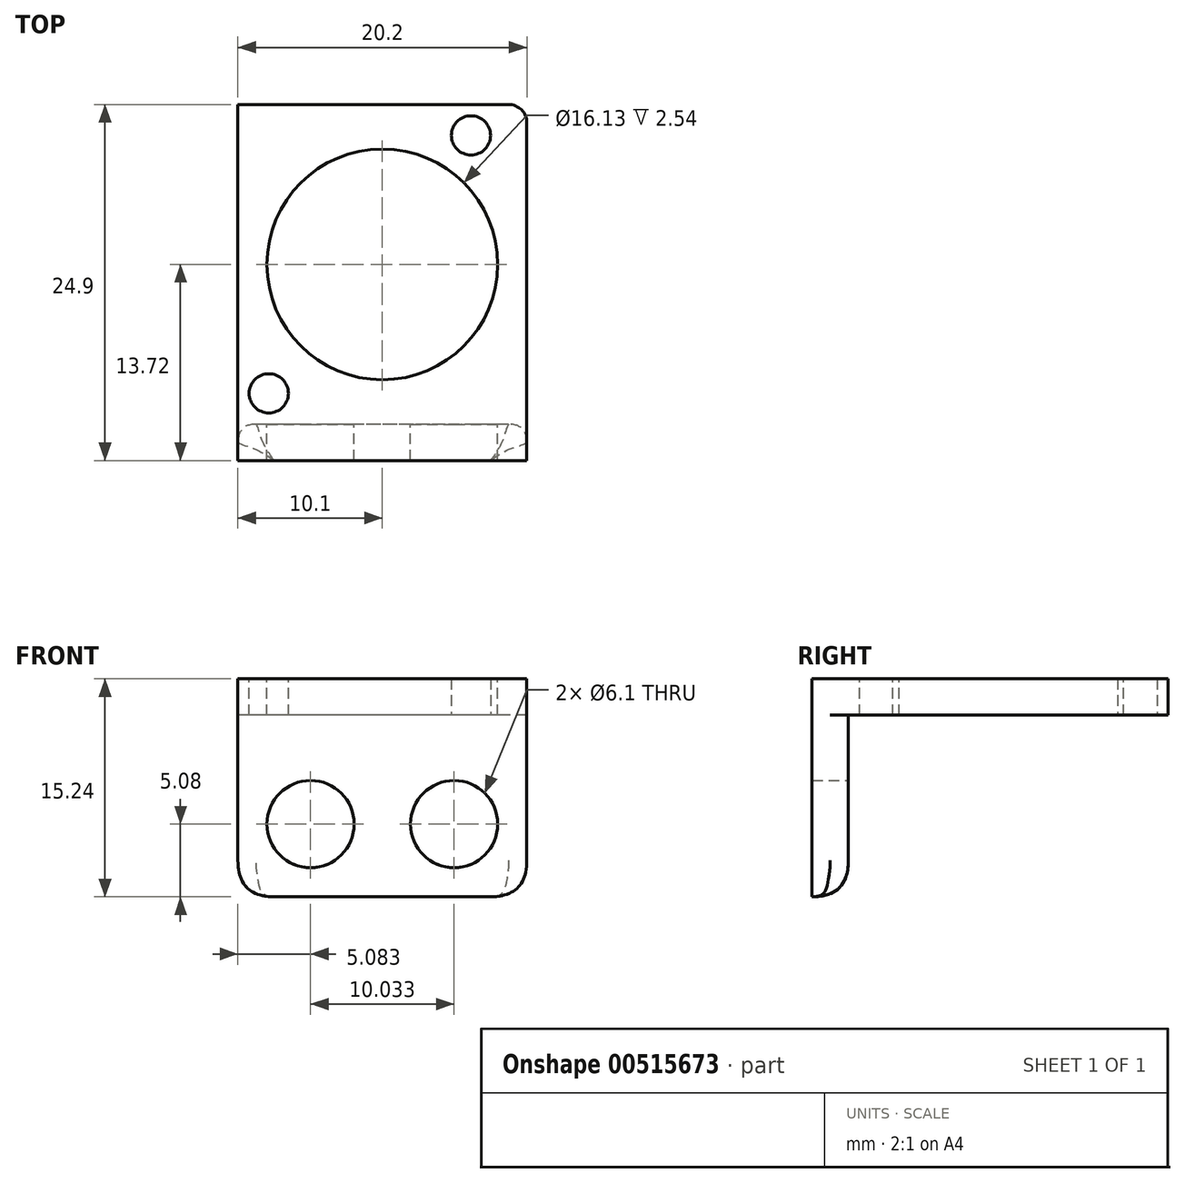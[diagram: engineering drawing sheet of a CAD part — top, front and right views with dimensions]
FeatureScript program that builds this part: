
annotation { "Feature Type Name" : "Feature", "Feature Type Description" : "" }
export const myFeature = defineFeature(function(context is Context, id is Id, definition is map)
    precondition{}
    {
        {
            var Q0;
            Q0=qCreatedBy(makeId("Top.planeOp"),FACE);
            var sketch = newSketch(context, id + "F0", { "sketchPlane" : qUnion([Q0])});
            skLineSegment(sketch, "E0.bottom", {"start": v(10.1, 11.18) * mm, "end": v(-10.1, 11.18) * mm});
            skLineSegment(sketch, "E0.top", {"start": v(10.1, -11.18) * mm, "end": v(-10.1, -11.18) * mm});
            skLineSegment(sketch, "E0.left", {"start": v(10.1, 11.18) * mm, "end": v(10.1, -11.18) * mm});
            skLineSegment(sketch, "E0.right", {"start": v(-10.1, 11.18) * mm, "end": v(-10.1, -11.18) * mm});
            skPoint(sketch, "E0.middle", {"position": v(0, 0) * mm});
            skSolve(sketch);
        }
        {
            var Q0;
            Q0=makeQuery(id+"F0.imprint","IMPRINT",FACE,{"disambiguationData":[TD([[makeQuery(id+"F0.imprint","IMPRINT",EDGE,{"derivedFrom":sQuery(id+"F0.wireOp",EDGE,"E0.bottom")}),1.0]])]});
            var sketch = newSketch(context, id + "F1", { "sketchPlane" : qUnion([Q0])});
            skCircle(sketch, "E1", {"center": v(6.2, 9.02) * mm, "radius": 1.37 * mm});
            skSolve(sketch);
        }
        {
            var Q0;
            Q0=makeQuery(id+"F1.imprint","IMPRINT",FACE,{"disambiguationData":[TD([[makeQuery(id+"F1.imprint","IMPRINT",EDGE,{"derivedFrom":sQuery(id+"F1.wireOp",EDGE,"E1")}),-1.0]])]});
            extrude(context, id + "F2", {"entities" : qUnion([Q0]), "depth" : 2.54 * mm, "offsetDistance" : 25.4 * mm});
        }
        {
            var Q0;
            Q0=makeQuery(id+"F2.opExtrude","CAP_FACE",FACE,{"disambiguationData":[OSD([sQuery(id+"F0.wireOp",EDGE,"E0.bottom"),sQuery(id+"F0.wireOp",EDGE,"E0.top"),sQuery(id+"F0.wireOp",EDGE,"E0.left"),sQuery(id+"F0.wireOp",EDGE,"E0.right"),sQuery(id+"F1.wireOp",EDGE,"E1")])],"isStart":false});
            var sketch = newSketch(context, id + "F3", { "sketchPlane" : qUnion([Q0])});
            skCircle(sketch, "E2", {"center": v(-7.94, -9.02) * mm, "radius": 1.37 * mm});
            skSolve(sketch);
        }
        {
            var Q0;
            Q0=makeQuery(id+"F3.imprint","IMPRINT",FACE,{"disambiguationData":[TD([[makeQuery(id+"F3.imprint","IMPRINT",EDGE,{"derivedFrom":sQuery(id+"F3.wireOp",EDGE,"E2")}),1.0]])]});
            extrude(context, id + "F4", {"entities" : qUnion([Q0]), "operationType" : NewBodyOperationType.REMOVE, "oppositeDirection" : true, "depth" : 2.54 * mm, "offsetDistance" : 25.4 * mm});
        }
        {
            var Q0;
            Q0=makeQuery(id+"F2.opExtrude","CAP_FACE",FACE,{"disambiguationData":[OSD([sQuery(id+"F0.wireOp",EDGE,"E0.bottom"),sQuery(id+"F0.wireOp",EDGE,"E0.top"),sQuery(id+"F0.wireOp",EDGE,"E0.left"),sQuery(id+"F0.wireOp",EDGE,"E0.right"),sQuery(id+"F1.wireOp",EDGE,"E1")])],"isStart":false});
            var sketch = newSketch(context, id + "F5", { "sketchPlane" : qUnion([Q0])});
            skCircle(sketch, "E3", {"center": v(0, 0) * mm, "radius": 8.06 * mm});
            skSolve(sketch);
        }
        {
            var Q0;
            Q0=makeQuery(id+"F5.imprint","IMPRINT",FACE,{"disambiguationData":[TD([[makeQuery(id+"F5.imprint","IMPRINT",EDGE,{"derivedFrom":sQuery(id+"F5.wireOp",EDGE,"E3")}),1.0]])]});
            extrude(context, id + "F6", {"entities" : qUnion([Q0]), "operationType" : NewBodyOperationType.REMOVE, "oppositeDirection" : true, "depth" : 2.54 * mm, "offsetDistance" : 25.4 * mm});
        }
        {
            var Q0;
            Q0=makeQuery(id+"F2.opExtrude","SWEPT_EDGE",EDGE,{"disambiguationData":[OSD([sQuery(id+"F0.wireOp",EDGE,"E0.bottom"),sQuery(id+"F0.wireOp",EDGE,"E0.left")])]});
            fillet(context, id + "F7", {"entities" : qUnion([Q0]), "radius" : 1.27 * mm, "tangentPropagation" : true, "allowEdgeOverflow" : false});
        }
        {
            var Q0;
            Q0=makeQuery(id+"F2.opExtrude","CAP_FACE",FACE,{"disambiguationData":[OSD([sQuery(id+"F0.wireOp",EDGE,"E0.bottom"),sQuery(id+"F0.wireOp",EDGE,"E0.top"),sQuery(id+"F0.wireOp",EDGE,"E0.left"),sQuery(id+"F0.wireOp",EDGE,"E0.right"),sQuery(id+"F1.wireOp",EDGE,"E1")])],"isStart":false});
            var sketch = newSketch(context, id + "F8", { "sketchPlane" : qUnion([Q0])});
            skLineSegment(sketch, "E4.bottom", {"start": v(-10.1, -11.18) * mm, "end": v(10.1, -11.18) * mm});
            skLineSegment(sketch, "E4.top", {"start": v(-10.1, -13.72) * mm, "end": v(10.1, -13.72) * mm});
            skLineSegment(sketch, "E4.left", {"start": v(-10.1, -11.18) * mm, "end": v(-10.1, -13.72) * mm});
            skLineSegment(sketch, "E4.right", {"start": v(10.1, -11.18) * mm, "end": v(10.1, -13.72) * mm});
            skSolve(sketch);
        }
        {
            var Q0;
            Q0=makeQuery(id+"F8.imprint","IMPRINT",FACE,{"disambiguationData":[TD([[makeQuery(id+"F8.imprint","IMPRINT",EDGE,{"derivedFrom":sQuery(id+"F8.wireOp",EDGE,"E4.top")}),1.0]])]});
            extrude(context, id + "F9", {"entities" : qUnion([Q0]), "operationType" : NewBodyOperationType.ADD, "oppositeDirection" : true, "depth" : 15.24 * mm, "offsetDistance" : 25.4 * mm});
        }
        {
            var Q0;
            Q0=makeQuery(id+"F9.opExtrude","SWEPT_FACE",FACE,{"disambiguationData":[OSD([sQuery(id+"F8.wireOp",EDGE,"E4.bottom")])]});
            var sketch = newSketch(context, id + "F10", { "sketchPlane" : qUnion([Q0])});
            skCircle(sketch, "E5", {"center": v(-5.02, -7.62) * mm, "radius": 3.05 * mm});
            skSolve(sketch);
        }
        {
            var Q0;
            Q0=makeQuery(id+"F10.imprint","IMPRINT",FACE,{"disambiguationData":[TD([[makeQuery(id+"F10.imprint","IMPRINT",EDGE,{"derivedFrom":sQuery(id+"F10.wireOp",EDGE,"E5")}),-1.0]])]});
            var sketch = newSketch(context, id + "F11", { "sketchPlane" : qUnion([Q0])});
            skCircle(sketch, "E6", {"center": v(5.02, -7.62) * mm, "radius": 3.05 * mm});
            skSolve(sketch);
        }
        {
            var Q0;
            Q0=makeQuery(id+"F10.imprint","IMPRINT",FACE,{"disambiguationData":[TD([[makeQuery(id+"F10.imprint","IMPRINT",EDGE,{"derivedFrom":sQuery(id+"F10.wireOp",EDGE,"E5")}),1.0]])]});
            extrude(context, id + "F12", {"entities" : qUnion([Q0]), "operationType" : NewBodyOperationType.REMOVE, "oppositeDirection" : true, "depth" : 2.54 * mm, "offsetDistance" : 25.4 * mm});
        }
        {
            var Q0;
            Q0=makeQuery(id+"F11.imprint","IMPRINT",FACE,{"disambiguationData":[TD([[makeQuery(id+"F11.imprint","IMPRINT",EDGE,{"derivedFrom":sQuery(id+"F11.wireOp",EDGE,"E6")}),1.0]])]});
            extrude(context, id + "F13", {"entities" : qUnion([Q0]), "operationType" : NewBodyOperationType.REMOVE, "oppositeDirection" : true, "depth" : 2.54 * mm, "offsetDistance" : 25.4 * mm});
        }
        {
            var Q0;
            Q0=makeQuery(id+"F9.opExtrude","CAP_EDGE",EDGE,{"disambiguationData":[OSD([sQuery(id+"F8.wireOp",EDGE,"E4.bottom")])],"isStart":false});
            var Q1;
            Q1=makeQuery(id+"F9.opExtrude","CAP_EDGE",EDGE,{"disambiguationData":[OSD([sQuery(id+"F8.wireOp",EDGE,"E4.left")])],"isStart":false});
            var Q2;
            Q2=makeQuery(id+"F9.opExtrude","CAP_EDGE",EDGE,{"disambiguationData":[OSD([sQuery(id+"F8.wireOp",EDGE,"E4.right")])],"isStart":false});
            fillet(context, id + "F14", {"entities" : qUnion([Q0, Q1, Q2]), "radius" : 2.54 * mm, "tangentPropagation" : true, "rho" : 0.5, "crossSection" : FilletCrossSection.CONIC, "allowEdgeOverflow" : false});
        }
        {
            var Q0;
            Q0=makeQuery(id+"F14.opFillet","BLEND_EDGE",EDGE,{"blendedFrom":[makeQuery(id+"F9.opExtrude","CAP_EDGE",EDGE,{"disambiguationData":[OSD([sQuery(id+"F8.wireOp",EDGE,"E4.bottom")])],"isStart":false}),makeQuery(id+"F9.opExtrude","CAP_EDGE",EDGE,{"disambiguationData":[OSD([sQuery(id+"F8.wireOp",EDGE,"E4.right")])],"isStart":false})],"blendedInto":[]});
            var Q1;
            Q1=makeQuery(id+"F14.opFillet","BLEND_EDGE",EDGE,{"blendedFrom":[makeQuery(id+"F9.opExtrude","CAP_EDGE",EDGE,{"disambiguationData":[OSD([sQuery(id+"F8.wireOp",EDGE,"E4.bottom")])],"isStart":false}),makeQuery(id+"F9.opExtrude","CAP_EDGE",EDGE,{"disambiguationData":[OSD([sQuery(id+"F8.wireOp",EDGE,"E4.left")])],"isStart":false})],"blendedInto":[]});
            fillet(context, id + "F15", {"entities" : qUnion([Q0, Q1]), "radius" : 1.27 * mm, "tangentPropagation" : true, "rho" : 0.5, "crossSection" : FilletCrossSection.CONIC, "allowEdgeOverflow" : false});
        }
    });
